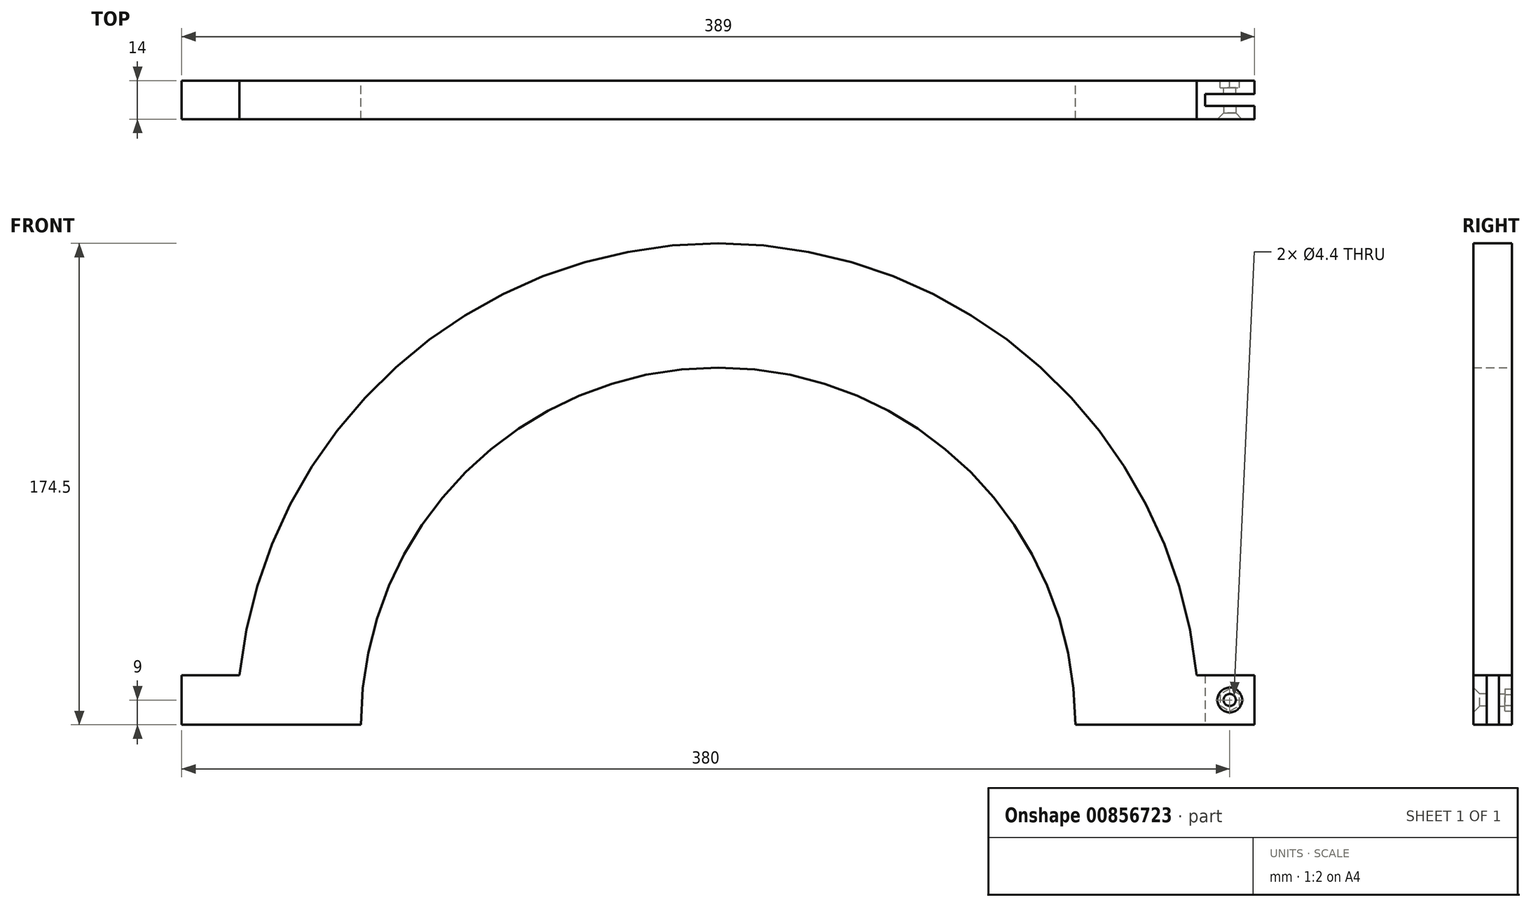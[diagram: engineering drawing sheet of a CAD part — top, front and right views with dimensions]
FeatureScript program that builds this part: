
annotation { "Feature Type Name" : "Feature", "Feature Type Description" : "" }
export const myFeature = defineFeature(function(context is Context, id is Id, definition is map)
    precondition{}
    {
        {
            var Q0;
            Q0=qCreatedBy(makeId("Front.planeOp"),FACE);
            var sketch = newSketch(context, id + "F0", { "sketchPlane" : qUnion([Q0])});
            skArc(sketch, "E0", {"start": v(174.5, 0) * mm, "mid": v(0, 174.5) * mm, "end": v(-174.5, 0) * mm});
            skArc(sketch, "E1", {"start": v(129.5, 0) * mm, "mid": v(0, 129.5) * mm, "end": v(-129.5, 0) * mm});
            skLineSegment(sketch, "E2", {"start": v(-174.5, 0) * mm, "end": v(-129.5, 0) * mm});
            skLineSegment(sketch, "E3.trimOffspring", {"start": v(129.5, 0) * mm, "end": v(174.5, 0) * mm});
            skLineSegment(sketch, "E4", {"start": v(-174.5, 0) * mm, "end": v(-174.5, -52.73) * mm, "construction": true});
            skLineSegment(sketch, "E5", {"start": v(0, 82.24) * mm, "end": v(0, -91.49) * mm, "construction": true});
            skLineSegment(sketch, "E6", {"start": v(174.5, 0) * mm, "end": v(194.5, 0) * mm});
            skLineSegment(sketch, "E7", {"start": v(194.5, 0) * mm, "end": v(194.5, 18) * mm});
            skLineSegment(sketch, "E8", {"start": v(194.5, 18) * mm, "end": v(173.57, 18) * mm});
            skLineSegment(sketch, "E9.MirrorCS", {"start": v(-194.5, 18) * mm, "end": v(-173.57, 18) * mm});
            skLineSegment(sketch, "E10.MirrorCS", {"start": v(-194.5, 0) * mm, "end": v(-194.5, 18) * mm});
            skLineSegment(sketch, "E11.MirrorCS", {"start": v(-174.5, 0) * mm, "end": v(-194.5, 0) * mm});
            skSolve(sketch);
        }
        {
            var Q0;
            Q0=qSketchRegion(id+"F0",true);
            extrude(context, id + "F1", {"entities" : qUnion([Q0]), "endBound" : BoundingType.SYMMETRIC, "depth" : 14 * mm, "offsetDistance" : 25 * mm});
        }
        {
            var Q0;
            Q0 = qSketchRegion(id + "F0", true);
            extrude(context, id + "F2", {"entities" : qUnion([Q0]), "operationType" : NewBodyOperationType.ADD, "endBound" : BoundingType.SYMMETRIC, "depth" : 12 * mm, "offsetDistance" : 25 * mm});
        }
        {
            var Q0;
            Q0=makeQuery(id+"F1.opExtrude","SWEPT_FACE",FACE,{"disambiguationData":[OSD([sQuery(id+"F0.wireOp",EDGE,"E7")])]});
            var sketch = newSketch(context, id + "F3", { "sketchPlane" : qUnion([Q0])});
            skLineSegment(sketch, "E12.bottom", {"start": v(-2.2, 18) * mm, "end": v(2.2, 18) * mm});
            skLineSegment(sketch, "E12.top", {"start": v(-2.2, 0) * mm, "end": v(2.2, 0) * mm});
            skLineSegment(sketch, "E12.left", {"start": v(-2.2, 18) * mm, "end": v(-2.2, 0) * mm});
            skLineSegment(sketch, "E12.right", {"start": v(2.2, 18) * mm, "end": v(2.2, 0) * mm});
            skSolve(sketch);
        }
        {
            var Q0;
            Q0 = qSketchRegion(id + "F3", true);
            extrude(context, id + "F4", {"entities" : qUnion([Q0]), "operationType" : NewBodyOperationType.REMOVE, "oppositeDirection" : true, "depth" : 18 * mm, "offsetDistance" : 25 * mm});
        }
        {
            var Q0;
            Q0=makeQuery(id+"F1.opExtrude","CAP_FACE",FACE,{"disambiguationData":[OSD([sQuery(id+"F0.wireOp",EDGE,"E0"),sQuery(id+"F0.wireOp",EDGE,"E1"),sQuery(id+"F0.wireOp",EDGE,"E2"),sQuery(id+"F0.wireOp",EDGE,"E3.trimOffspring"),sQuery(id+"F0.wireOp",EDGE,"E6"),sQuery(id+"F0.wireOp",EDGE,"E7"),sQuery(id+"F0.wireOp",EDGE,"E8"),sQuery(id+"F0.wireOp",EDGE,"E9.MirrorCS"),sQuery(id+"F0.wireOp",EDGE,"E10.MirrorCS"),sQuery(id+"F0.wireOp",EDGE,"E11.MirrorCS")])],"isStart":false});
            var sketch = newSketch(context, id + "F5", { "sketchPlane" : qUnion([Q0])});
            skCircle(sketch, "E13", {"center": v(185.5, 9) * mm, "radius": 3.22 * mm});
            skSolve(sketch);
        }
        {
            var Q0;
            Q0=sQuery(id+"F5.wireOp",VERTEX,"E13.center");
            var Q1;
            Q1=makeQuery(id+"F1.opExtrude","SWEPT_BODY",BODY,{"disambiguationData":[OSD([sQuery(id+"F0.wireOp",EDGE,"E0"),sQuery(id+"F0.wireOp",EDGE,"E1"),sQuery(id+"F0.wireOp",EDGE,"E2"),sQuery(id+"F0.wireOp",EDGE,"E3.trimOffspring"),sQuery(id+"F0.wireOp",EDGE,"E6"),sQuery(id+"F0.wireOp",EDGE,"E7"),sQuery(id+"F0.wireOp",EDGE,"E8"),sQuery(id+"F0.wireOp",EDGE,"E9.MirrorCS"),sQuery(id+"F0.wireOp",EDGE,"E10.MirrorCS"),sQuery(id+"F0.wireOp",EDGE,"E11.MirrorCS")])]});
            hole(context, id + "F6", {"style" : HoleStyle.C_SINK, "endStyle" : HoleEndStyle.BLIND, "standardTappedOrClearance" : lookupTablePath({ "fit" : "Normal", "standard" : "ISO", "size" : "M4", "type" : "Clearance" }), "standardBlindInLast" : lookupTablePath({ "fit" : "Standard", "standard" : "ISO", "size" : "M4", "type" : "Clearance" }), "holeDiameter" : 4.4 * mm, "cSinkDiameter" : 8.96 * mm, "cSinkAngle" : 90 * degree, "majorDiameter" : 4 * mm, "holeDepth" : 5 * mm, "isTappedThrough" : true, "tappedDepth" : 12 * mm, "tapClearance" : 3, "startFromSketch" : true, "locations" : qUnion([Q0]), "scope" : qUnion([Q1])});
        }
        {
            var Q0;
            Q0=makeQuery(id+"F1.opExtrude","CAP_FACE",FACE,{"disambiguationData":[OSD([sQuery(id+"F0.wireOp",EDGE,"E0"),sQuery(id+"F0.wireOp",EDGE,"E1"),sQuery(id+"F0.wireOp",EDGE,"E2"),sQuery(id+"F0.wireOp",EDGE,"E3.trimOffspring"),sQuery(id+"F0.wireOp",EDGE,"E6"),sQuery(id+"F0.wireOp",EDGE,"E7"),sQuery(id+"F0.wireOp",EDGE,"E8"),sQuery(id+"F0.wireOp",EDGE,"E9.MirrorCS"),sQuery(id+"F0.wireOp",EDGE,"E10.MirrorCS"),sQuery(id+"F0.wireOp",EDGE,"E11.MirrorCS")])],"isStart":true});
            var sketch = newSketch(context, id + "F7", { "sketchPlane" : qUnion([Q0])});
            skLineSegment(sketch, "E14.0", {"start": v(-189, 6.98) * mm, "end": v(-189, 11.02) * mm});
            skLineSegment(sketch, "E14.1", {"start": v(-189, 11.02) * mm, "end": v(-185.5, 13.04) * mm});
            skLineSegment(sketch, "E14.2", {"start": v(-185.5, 13.04) * mm, "end": v(-182, 11.02) * mm});
            skLineSegment(sketch, "E14.3", {"start": v(-182, 11.02) * mm, "end": v(-182, 6.98) * mm});
            skLineSegment(sketch, "E14.4", {"start": v(-182, 6.98) * mm, "end": v(-185.5, 4.96) * mm});
            skLineSegment(sketch, "E14.5", {"start": v(-185.5, 4.96) * mm, "end": v(-189, 6.98) * mm});
            skPoint(sketch, "E14.0.midPoint", {"position": v(-189, 9) * mm});
            skSolve(sketch);
        }
        {
            var Q0;
            Q0 = qSketchRegion(id + "F7", true);
            extrude(context, id + "F8", {"entities" : qUnion([Q0]), "operationType" : NewBodyOperationType.REMOVE, "oppositeDirection" : true, "depth" : 2.6 * mm, "offsetDistance" : 25 * mm});
        }
        {
            var Q0;
            Q0=makeQuery(id+"F8.boolean.opBoolean","COPY",FACE,{"derivedFrom":makeQuery(id+"F8.opExtrude","CAP_FACE",FACE,{"disambiguationData":[OSD([sQuery(id+"F7.wireOp",EDGE,"E14.0"),sQuery(id+"F7.wireOp",EDGE,"E14.1"),sQuery(id+"F7.wireOp",EDGE,"E14.2"),sQuery(id+"F7.wireOp",EDGE,"E14.3"),sQuery(id+"F7.wireOp",EDGE,"E14.4"),sQuery(id+"F7.wireOp",EDGE,"E14.5")])],"isStart":false})});
            var sketch = newSketch(context, id + "F9", { "sketchPlane" : qUnion([Q0])});
            skCircle(sketch, "E15", {"center": v(-185.5, 9) * mm, "radius": 2.2 * mm});
            skSolve(sketch);
        }
        {
            var Q0;
            Q0 = qSketchRegion(id + "F9", true);
            extrude(context, id + "F10", {"entities" : qUnion([Q0]), "operationType" : NewBodyOperationType.REMOVE, "oppositeDirection" : true, "depth" : 2.3 * mm, "offsetDistance" : 25 * mm});
        }
    });
